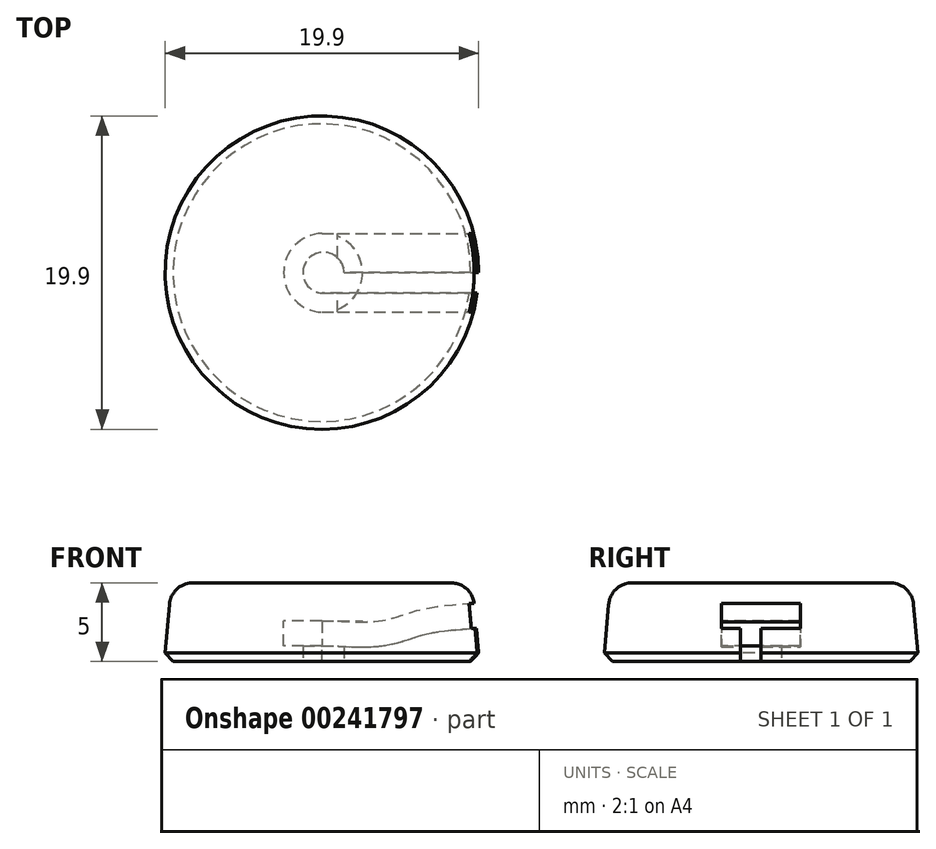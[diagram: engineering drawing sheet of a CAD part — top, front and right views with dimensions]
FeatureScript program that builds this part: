
annotation { "Feature Type Name" : "Feature", "Feature Type Description" : "" }
export const myFeature = defineFeature(function(context is Context, id is Id, definition is map)
    precondition{}
    {
        {
            var Q0;
            Q0=qCreatedBy(makeId("Top.planeOp"),FACE);
            var sketch = newSketch(context, id + "F0", { "sketchPlane" : qUnion([Q0])});
            skCircle(sketch, "E0", {"center": v(0, 0) * mm, "radius": 10 * mm});
            skSolve(sketch);
        }
        {
            var Q0;
            Q0=makeQuery(id+"F0.imprint","IMPRINT",FACE,{"disambiguationData":[TD([[makeQuery(id+"F0.imprint","IMPRINT",EDGE,{"derivedFrom":sQuery(id+"F0.wireOp",EDGE,"E0")}),1.0]])]});
            extrude(context, id + "F1", {"entities" : qUnion([Q0]), "depth" : 5 * mm, "hasDraft" : true, "draftAngle" : 5 * degree, "draftPullDirection" : true});
        }
        {
            var Q0;
            Q0=makeQuery(id+"F1.opExtrude","CAP_EDGE",EDGE,{"disambiguationData":[OSD([sQuery(id+"F0.wireOp",EDGE,"E0")])],"isStart":false});
            fillet(context, id + "F2", {"entities" : qUnion([Q0]), "radius" : 1.5 * mm, "tangentPropagation" : true, "allowEdgeOverflow" : false});
        }
        {
            var Q0;
            Q0=makeQuery(id+"F1.opExtrude","CAP_EDGE",EDGE,{"disambiguationData":[OSD([sQuery(id+"F0.wireOp",EDGE,"E0")])],"isStart":true});
            chamfer(context, id + "F3", {"entities" : qUnion([Q0]), "width" : .5 * mm, "tangentPropagation" : true});
        }
        {
            var Q0;
            Q0=qCreatedBy(makeId("Right.planeOp"),FACE);
            var sketch = newSketch(context, id + "F4", { "sketchPlane" : qUnion([Q0])});
            skLineSegment(sketch, "E1.bottom", {"start": v(-45.6, 41.58) * mm, "end": v(-40.6, 41.58) * mm});
            skLineSegment(sketch, "E1.top", {"start": v(-45.6, 39.98) * mm, "end": v(-40.6, 39.98) * mm});
            skLineSegment(sketch, "E1.left", {"start": v(-45.6, 41.58) * mm, "end": v(-45.6, 39.98) * mm});
            skLineSegment(sketch, "E1.right", {"start": v(-40.6, 41.58) * mm, "end": v(-40.6, 39.98) * mm});
            skLineSegment(sketch, "E2.bottom", {"start": v(-43.1, 39.98) * mm, "end": v(-41.8, 39.98) * mm});
            skLineSegment(sketch, "E2.top", {"start": v(-43.1, 29.98) * mm, "end": v(-41.8, 29.98) * mm});
            skLineSegment(sketch, "E2.left", {"start": v(-43.1, 39.98) * mm, "end": v(-43.1, 29.98) * mm});
            skLineSegment(sketch, "E2.right", {"start": v(-41.8, 39.98) * mm, "end": v(-41.8, 29.98) * mm});
            skLineSegment(sketch, "E3.bottom", {"start": v(-43.1, 29.98) * mm, "end": v(-44.4, 29.98) * mm});
            skLineSegment(sketch, "E3.top", {"start": v(-43.1, 39.98) * mm, "end": v(-44.4, 39.98) * mm});
            skLineSegment(sketch, "E3.left", {"start": v(-43.1, 29.98) * mm, "end": v(-43.1, 39.98) * mm});
            skLineSegment(sketch, "E3.right", {"start": v(-44.4, 29.98) * mm, "end": v(-44.4, 39.98) * mm});
            skSolve(sketch);
        }
        {
            var Q0;
            Q0=qCreatedBy(makeId("Front.planeOp"),FACE);
            var sketch = newSketch(context, id + "F5", { "sketchPlane" : qUnion([Q0])});
            skFitSpline(sketch, "E4", {"points": [v(0, 40.18) * mm, v(3.69, 40.37) * mm, v(6, 41.03) * mm, v(12.09, 41.4) * mm], "startDerivative": vector(15.96, -1.05) * mm, "endDerivative": vector(13.49, 0.06) * mm});
            skSolve(sketch);
        }
        {
            var Q0;
            Q0=makeQuery(id+"F4.imprint","IMPRINT",FACE,{"disambiguationData":[TD([[makeQuery(id+"F4.imprint","IMPRINT",EDGE,{"derivedFrom":sQuery(id+"F4.wireOp",EDGE,"E3.bottom")}),-1.0]])]});
            var Q1;
            Q1=makeQuery(id+"F4.imprint","IMPRINT",FACE,{"disambiguationData":[TD([[makeQuery(id+"F4.imprint","IMPRINT",EDGE,{"derivedFrom":sQuery(id+"F4.wireOp",EDGE,"E2.bottom")}),-1.0]])]});
            var Q2;
            Q2=makeQuery(id+"F4.imprint","IMPRINT",FACE,{"disambiguationData":[TD([[makeQuery(id+"F4.imprint","IMPRINT",EDGE,{"derivedFrom":sQuery(id+"F4.wireOp",EDGE,"E1.bottom")}),-1.0]])]});
            var Q3;
            Q3=sQuery(id+"F5.wireOp",EDGE,"E4");
            sweep(context, id + "F6", {"profiles" : qUnion([Q0, Q1, Q2]), "path" : qUnion([Q3])});
        }
        {
            var Q0;
            Q0=makeQuery(id+"F6.opSweep","CAP_FACE",FACE,{"disambiguationData":[OSD([sQuery(id+"F4.wireOp",EDGE,"E1.bottom"),sQuery(id+"F4.wireOp",EDGE,"E1.top"),sQuery(id+"F4.wireOp",EDGE,"E1.left"),sQuery(id+"F4.wireOp",EDGE,"E1.right"),sQuery(id+"F4.wireOp",EDGE,"E2.top"),sQuery(id+"F4.wireOp",EDGE,"E2.right"),sQuery(id+"F4.wireOp",EDGE,"E3.bottom"),sQuery(id+"F4.wireOp",EDGE,"E3.right"),sQuery(id+"F5.wireOp",VERTEX,"E4.start")])],"isStart":true});
            extrude(context, id + "F7", {"entities" : qUnion([Q0]), "operationType" : NewBodyOperationType.ADD, "depth" : 1 * mm});
        }
        {
            var Q0;
            Q0=makeQuery(id+"F7.opExtrude","SWEPT_FACE",FACE,{"disambiguationData":[OSD([sQuery(id+"F4.wireOp",EDGE,"E2.top"),sQuery(id+"F4.wireOp",EDGE,"E3.bottom"),sQuery(id+"F5.wireOp",VERTEX,"E4.start")])]});
            var sketch = newSketch(context, id + "F8", { "sketchPlane" : qUnion([Q0])});
            skCircle(sketch, "E5", {"center": v(-0.9, 43.1) * mm, "radius": 1.3 * mm});
            skPoint(sketch, "E5.first.point", {"position": v(-1, 44.4) * mm});
            skPoint(sketch, "E5.second.point", {"position": v(-1, 41.8) * mm});
            skPoint(sketch, "E5.third.point", {"position": v(-2.2, 43.1) * mm});
            skPoint(sketch, "E5.third.point.positionSnap0", {"position": v(-1, 43.1) * mm});
            skSolve(sketch);
        }
        {
            var Q0;
            {var subQ1=sQuery(id+"F4.wireOp",EDGE,"E3.bottom");var subQ2=sQuery(id+"F4.wireOp",EDGE,"E2.top");var subQ3=makeQuery(id+"F7.opExtrude","CAP_EDGE",EDGE,{"disambiguationData":[OSD([subQ2,subQ1,sQuery(id+"F5.wireOp",VERTEX,"E4.start")])],"isStart":false});Q0=makeQuery(id+"F8.imprint","IMPRINT",FACE,{"disambiguationData":[TD([[makeQuery(id+"F8.imprint","IMPRINT",EDGE,{"derivedFrom":subQ3}),-1.0]])]});}
            extrude(context, id + "F9", {"entities" : qUnion([Q0]), "operationType" : NewBodyOperationType.ADD, "oppositeDirection" : true, "depth" : 11.6 * mm});
        }
        {
            var Q0;
            {var subQ0=sQuery(id+"F5.wireOp",VERTEX,"E4.start");Q0=makeQuery(id+"F9.boolean.opBoolean","MERGE",FACE,{"derivedFrom":[makeQuery(id+"F7.opExtrude","SWEPT_FACE",FACE,{"disambiguationData":[OSD([sQuery(id+"F4.wireOp",EDGE,"E1.bottom"),subQ0])]}),makeQuery(id+"F9.opExtrude","CAP_FACE",FACE,{"disambiguationData":[OSD([sQuery(id+"F4.wireOp",EDGE,"E2.top"),sQuery(id+"F4.wireOp",EDGE,"E3.bottom"),subQ0,sQuery(id+"F8.wireOp",EDGE,"E5")])],"isStart":false})]});}
            var sketch = newSketch(context, id + "F10", { "sketchPlane" : qUnion([Q0])});
            skCircle(sketch, "E6", {"center": v(-0.92, -43.1) * mm, "radius": 2.5 * mm});
            skPoint(sketch, "E6.first.point", {"position": v(-1, -45.6) * mm});
            skPoint(sketch, "E6.second.point", {"position": v(-1, -40.6) * mm});
            skPoint(sketch, "E6.third.point", {"position": v(-3.42, -43.1) * mm});
            skPoint(sketch, "E6.third.point.positionSnap0", {"position": v(-2.2, -43.1) * mm});
            skSolve(sketch);
        }
        {
            var Q0;
            {var subQ9=sQuery(id+"F8.wireOp",EDGE,"E5");Q0=makeQuery(id+"F10.imprint","IMPRINT",FACE,{"disambiguationData":[TD([[makeQuery(id+"F10.imprint","IMPRINT",EDGE,{"derivedFrom":makeQuery(id+"F9.opExtrude","CAP_EDGE",EDGE,{"disambiguationData":[OSD([subQ9])],"isStart":false})}),1.0]])]});}
            extrude(context, id + "F11", {"entities" : qUnion([Q0]), "operationType" : NewBodyOperationType.ADD, "oppositeDirection" : true, "depth" : 1.6 * mm});
        }
        {
            var Q0;
            Q0=makeQuery(id+"F6.opSweep","SWEPT_BODY",BODY,{"disambiguationData":[OSD([sQuery(id+"F4.wireOp",EDGE,"E1.bottom"),sQuery(id+"F4.wireOp",EDGE,"E1.top"),sQuery(id+"F4.wireOp",EDGE,"E1.left"),sQuery(id+"F4.wireOp",EDGE,"E1.right"),sQuery(id+"F4.wireOp",EDGE,"E2.top"),sQuery(id+"F4.wireOp",EDGE,"E2.right"),sQuery(id+"F4.wireOp",EDGE,"E3.bottom"),sQuery(id+"F4.wireOp",EDGE,"E3.right"),sQuery(id+"F5.wireOp",EDGE,"E4")])]});
            transform(context, id + "F12", {"entities" : qUnion([Q0]), "transformType" : TransformType.TRANSLATION_3D, "dx" : 1 * mm, "dy" : 43.1 * mm, "dz" : -39 * mm, "makeCopy" : false});
        }
        {
            var Q0;
            Q0=makeQuery(id+"F6.opSweep","SWEPT_BODY",BODY,{"disambiguationData":[OSD([sQuery(id+"F4.wireOp",EDGE,"E1.bottom"),sQuery(id+"F4.wireOp",EDGE,"E1.top"),sQuery(id+"F4.wireOp",EDGE,"E1.left"),sQuery(id+"F4.wireOp",EDGE,"E1.right"),sQuery(id+"F4.wireOp",EDGE,"E2.top"),sQuery(id+"F4.wireOp",EDGE,"E2.right"),sQuery(id+"F4.wireOp",EDGE,"E3.bottom"),sQuery(id+"F4.wireOp",EDGE,"E3.right"),sQuery(id+"F5.wireOp",EDGE,"E4")])]});
            var Q1;
            Q1=makeQuery(id+"F1.opExtrude","SWEPT_BODY",BODY,{"disambiguationData":[OSD([sQuery(id+"F0.wireOp",EDGE,"E0")])]});
            booleanBodies(context, id + "F13", {"operationType" : BooleanOperationType.SUBTRACTION, "tools" : qUnion([Q0]), "targets" : qUnion([Q1])});
        }
    });
